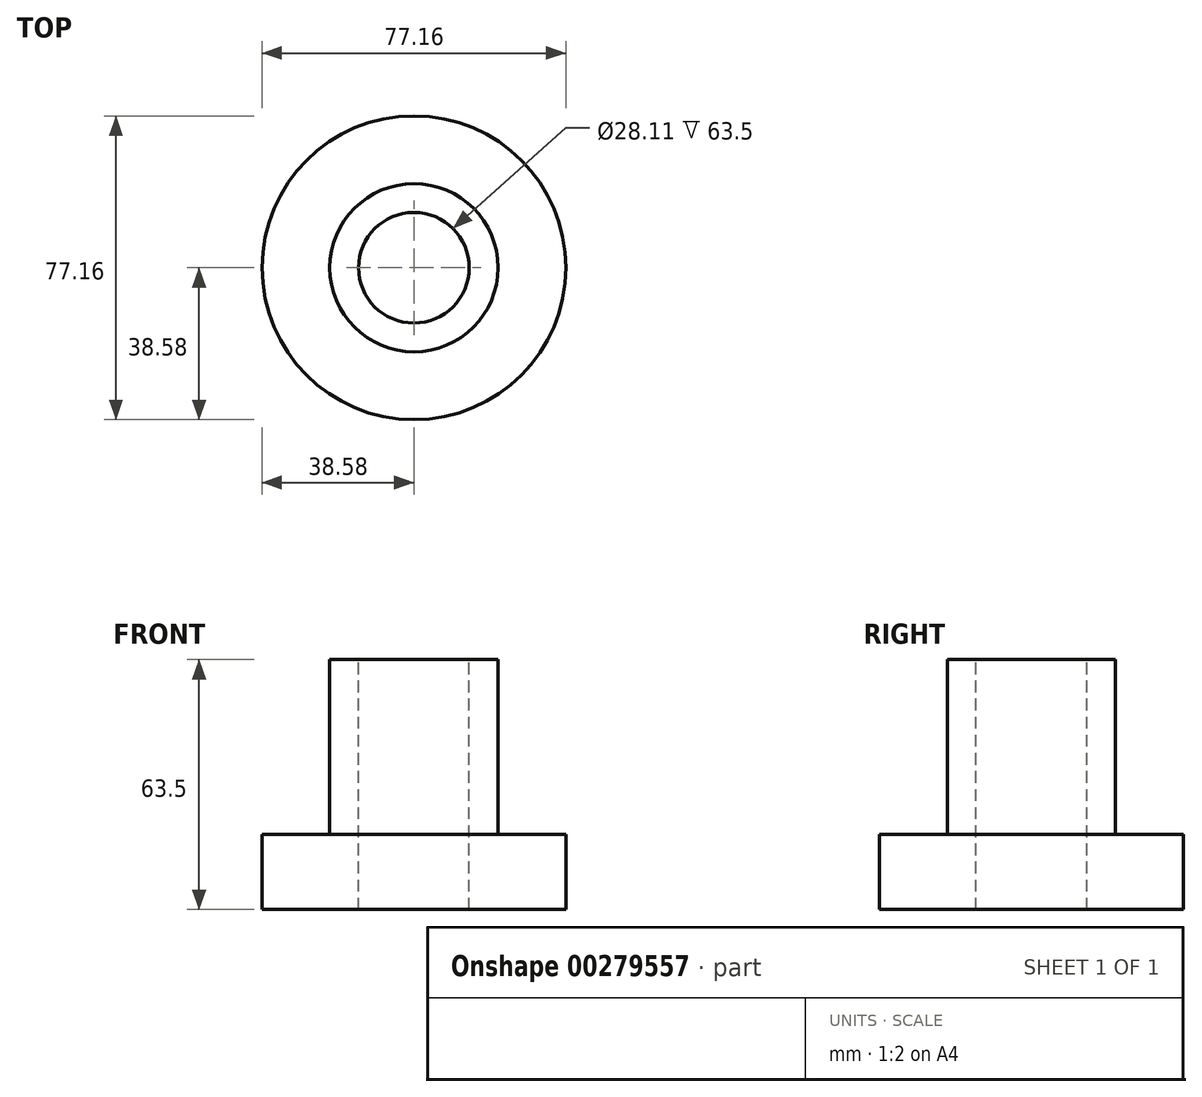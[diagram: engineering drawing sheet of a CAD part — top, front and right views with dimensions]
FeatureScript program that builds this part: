
annotation { "Feature Type Name" : "Feature", "Feature Type Description" : "" }
export const myFeature = defineFeature(function(context is Context, id is Id, definition is map)
    precondition{}
    {
        {
            var Q0;
            Q0=qCreatedBy(makeId("Top.planeOp"),FACE);
            var sketch = newSketch(context, id + "F0", { "sketchPlane" : qUnion([Q0])});
            skCircle(sketch, "E0", {"center": v(0, 0) * mm, "radius": 38.58 * mm});
            skSolve(sketch);
        }
        {
            var Q0;
            Q0=makeQuery(id+"F0.imprint","IMPRINT",FACE,{"disambiguationData":[TD([[makeQuery(id+"F0.imprint","IMPRINT",EDGE,{"derivedFrom":sQuery(id+"F0.wireOp",EDGE,"E0")}),1.0]])]});
            extrude(context, id + "F1", {"entities" : qUnion([Q0]), "depth" : 19.05 * mm});
        }
        {
            var Q0;
            Q0=makeQuery(id+"F1.opExtrude","CAP_FACE",FACE,{"disambiguationData":[OSD([sQuery(id+"F0.wireOp",EDGE,"E0")])],"isStart":false});
            var sketch = newSketch(context, id + "F2", { "sketchPlane" : qUnion([Q0])});
            skCircle(sketch, "E1", {"center": v(0, 0) * mm, "radius": 21.37 * mm});
            skSolve(sketch);
        }
        {
            var Q0;
            Q0=makeQuery(id+"F2.imprint","IMPRINT",FACE,{"disambiguationData":[TD([[makeQuery(id+"F2.imprint","IMPRINT",EDGE,{"derivedFrom":sQuery(id+"F2.wireOp",EDGE,"E1")}),1.0]])]});
            extrude(context, id + "F3", {"entities" : qUnion([Q0]), "operationType" : NewBodyOperationType.ADD, "depth" : 44.45 * mm});
        }
        {
            var Q0;
            Q0=makeQuery(id+"F3.opExtrude","CAP_FACE",FACE,{"disambiguationData":[OSD([sQuery(id+"F2.wireOp",EDGE,"E1")])],"isStart":false});
            var sketch = newSketch(context, id + "F4", { "sketchPlane" : qUnion([Q0])});
            skCircle(sketch, "E2", {"center": v(0, 0) * mm, "radius": 14.05 * mm});
            skSolve(sketch);
        }
        {
            var Q0;
            Q0=makeQuery(id+"F4.imprint","IMPRINT",FACE,{"disambiguationData":[TD([[makeQuery(id+"F4.imprint","IMPRINT",EDGE,{"derivedFrom":sQuery(id+"F4.wireOp",EDGE,"E2")}),1.0]])]});
            extrude(context, id + "F5", {"entities" : qUnion([Q0]), "operationType" : NewBodyOperationType.ADD, "oppositeDirection" : true, "depth" : 63.5 * mm});
        }
        {
            var Q0;
            Q0 = qSketchRegion(id + "F4", true);
            extrude(context, id + "F6", {"entities" : qUnion([Q0]), "operationType" : NewBodyOperationType.REMOVE, "oppositeDirection" : true, "depth" : 63.5 * mm});
        }
    });
